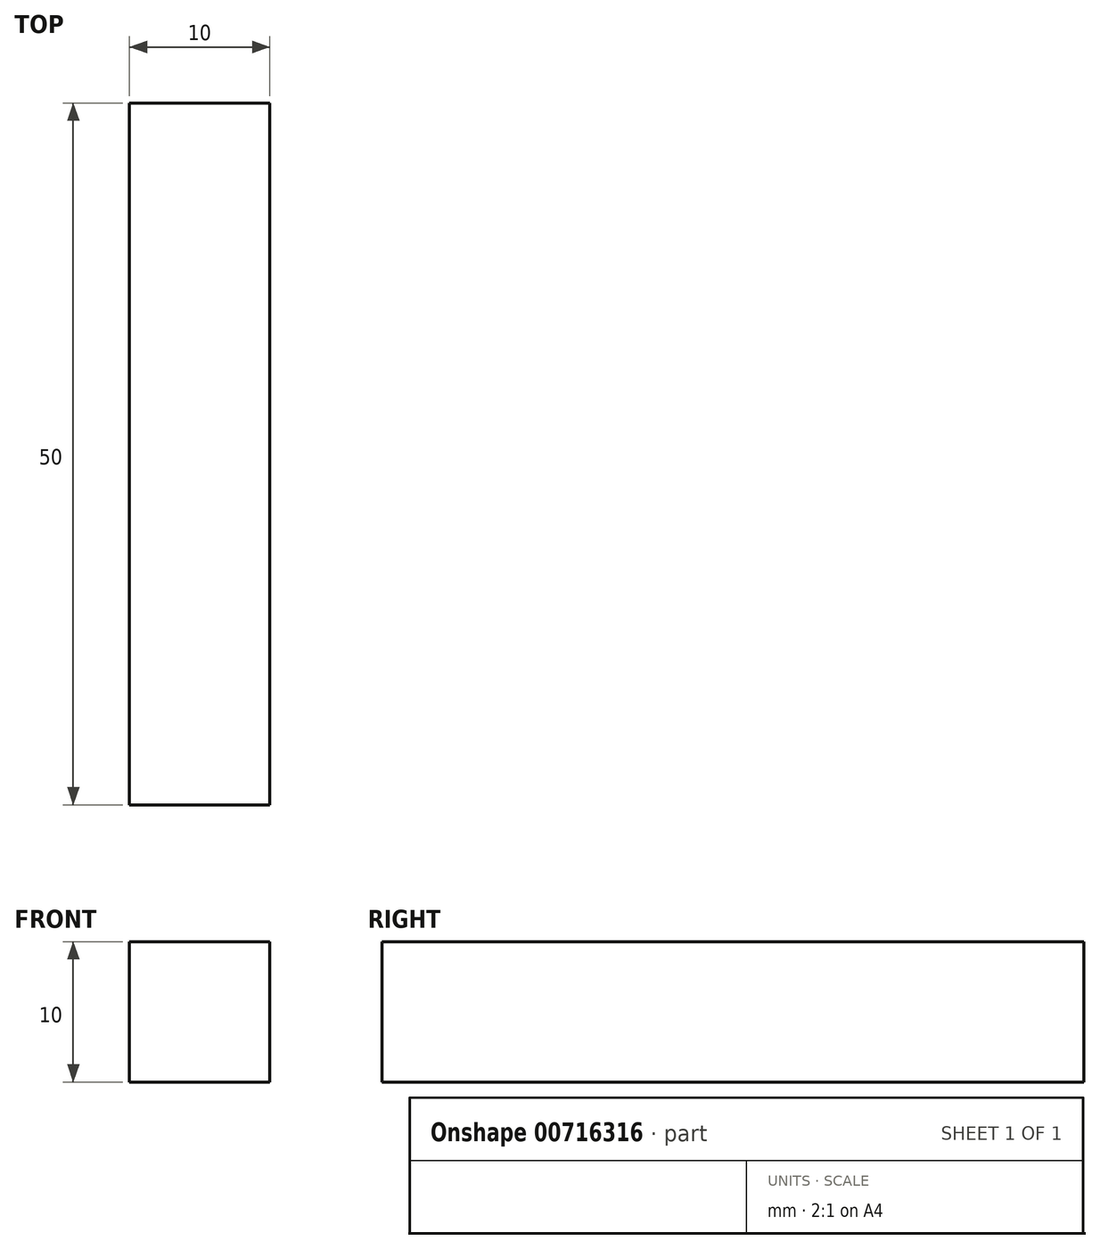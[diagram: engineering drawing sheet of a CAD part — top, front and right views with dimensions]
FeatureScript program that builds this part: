
annotation { "Feature Type Name" : "Feature", "Feature Type Description" : "" }
export const myFeature = defineFeature(function(context is Context, id is Id, definition is map)
    precondition{}
    {
        {
            var Q0;
            Q0=qCreatedBy(makeId("Top.planeOp"),FACE);
            var sketch = newSketch(context, id + "F0", { "sketchPlane" : qUnion([Q0])});
            skLineSegment(sketch, "E0.bottom", {"start": v(0, 0) * mm, "end": v(10, 0) * mm});
            skLineSegment(sketch, "E0.top", {"start": v(0, -50) * mm, "end": v(10, -50) * mm});
            skLineSegment(sketch, "E0.left", {"start": v(0, 0) * mm, "end": v(0, -50) * mm});
            skLineSegment(sketch, "E0.right", {"start": v(10, 0) * mm, "end": v(10, -50) * mm});
            skSolve(sketch);
        }
        {
            var Q0;
            Q0=makeQuery(id+"F0.imprint","IMPRINT",FACE,{"disambiguationData":[TD([[makeQuery(id+"F0.imprint","IMPRINT",EDGE,{"derivedFrom":sQuery(id+"F0.wireOp",EDGE,"E0.bottom")}),-1.0]])]});
            extrude(context, id + "F1", {"entities" : qUnion([Q0]), "depth" : 10 * mm, "offsetDistance" : 25 * mm});
        }
    });
